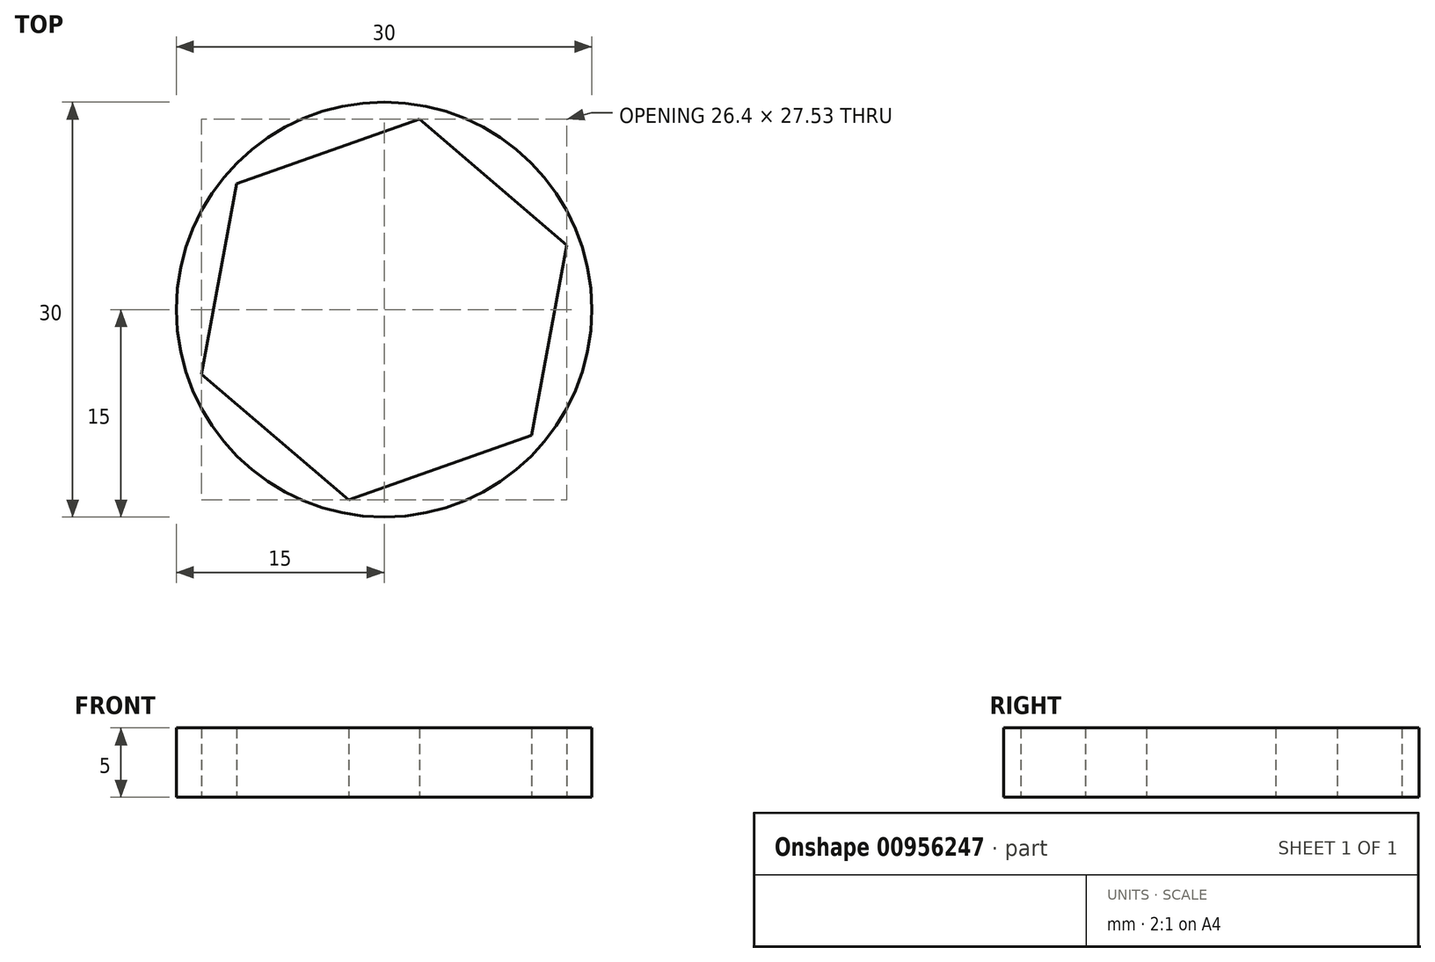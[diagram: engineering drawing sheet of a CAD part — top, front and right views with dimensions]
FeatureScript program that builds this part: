
annotation { "Feature Type Name" : "Feature", "Feature Type Description" : "" }
export const myFeature = defineFeature(function(context is Context, id is Id, definition is map)
    precondition{}
    {
        {
            var Q0;
            Q0=qCreatedBy(makeId("Top.planeOp"),FACE);
            var sketch = newSketch(context, id + "F0", { "sketchPlane" : qUnion([Q0])});
            skCircle(sketch, "E0", {"center": v(0, 0) * mm, "radius": 15 * mm});
            skCircle(sketch, "E1.cCircle", {"center": v(0, 0) * mm, "radius": 14 * mm, "construction": true});
            skLineSegment(sketch, "E1.0", {"start": v(10.43, 9.34) * mm, "end": v(13.3, -4.37) * mm});
            skLineSegment(sketch, "E1.1", {"start": v(13.3, -4.37) * mm, "end": v(2.87, -13.7) * mm});
            skLineSegment(sketch, "E1.2", {"start": v(2.87, -13.7) * mm, "end": v(-10.43, -9.34) * mm});
            skLineSegment(sketch, "E1.3", {"start": v(-10.43, -9.34) * mm, "end": v(-13.3, 4.37) * mm});
            skLineSegment(sketch, "E1.4", {"start": v(-13.3, 4.37) * mm, "end": v(-2.87, 13.7) * mm});
            skLineSegment(sketch, "E1.5", {"start": v(-2.87, 13.7) * mm, "end": v(10.43, 9.34) * mm});
            skSolve(sketch);
        }
        {
            var Q0;
            Q0=makeQuery(id+"F0.imprint","IMPRINT",FACE,{"disambiguationData":[TD([[makeQuery(id+"F0.imprint","IMPRINT",EDGE,{"derivedFrom":sQuery(id+"F0.wireOp",EDGE,"E1.0")}),-1.0]])]});
            var Q1;
            Q1=makeQuery(id+"F0.imprint","IMPRINT",FACE,{"disambiguationData":[TD([[makeQuery(id+"F0.imprint","IMPRINT",EDGE,{"derivedFrom":sQuery(id+"F0.wireOp",EDGE,"E0")}),1.0]])]});
            extrude(context, id + "F1", {"entities" : qUnion([Q0, Q1]), "depth" : 5 * mm, "offsetDistance" : 25 * mm});
        }
        {
            var Q0;
            Q0=makeQuery(id+"F1.opExtrude","CAP_FACE",FACE,{"disambiguationData":[OSD([sQuery(id+"F0.wireOp",EDGE,"E0")])],"isStart":true});
            var sketch = newSketch(context, id + "F2", { "sketchPlane" : qUnion([Q0])});
            skCircle(sketch, "E2.cCircle", {"center": v(0, 0) * mm, "radius": 14 * mm, "construction": true});
            skLineSegment(sketch, "E2.0", {"start": v(-10.64, -9.1) * mm, "end": v(-13.2, 4.67) * mm});
            skLineSegment(sketch, "E2.1", {"start": v(-13.2, 4.67) * mm, "end": v(-2.56, 13.76) * mm});
            skLineSegment(sketch, "E2.2", {"start": v(-2.56, 13.76) * mm, "end": v(10.64, 9.1) * mm});
            skLineSegment(sketch, "E2.3", {"start": v(10.64, 9.1) * mm, "end": v(13.2, -4.67) * mm});
            skLineSegment(sketch, "E2.4", {"start": v(13.2, -4.67) * mm, "end": v(2.56, -13.76) * mm});
            skLineSegment(sketch, "E2.5", {"start": v(2.56, -13.76) * mm, "end": v(-10.64, -9.1) * mm});
            skSolve(sketch);
        }
        {
            var Q0;
            Q0=makeQuery(id+"F2.imprint","IMPRINT",FACE,{"disambiguationData":[TD([[makeQuery(id+"F2.imprint","IMPRINT",EDGE,{"derivedFrom":sQuery(id+"F2.wireOp",EDGE,"E2.0")}),-1.0]])]});
            extrude(context, id + "F3", {"entities" : qUnion([Q0]), "operationType" : NewBodyOperationType.REMOVE, "oppositeDirection" : true, "depth" : 25 * mm, "offsetDistance" : 25 * mm});
        }
    });
